# Revit family: lady_b_lady_b_585
name_source: partatom
category: Leuchten
revit_build: Autodesk Revit 2016 (Build: 20190508_0715(x64)
units: mm (PartAtom-declared; Revit-internal decimal feet)

## family parameters
Basisbauteil = Fläche
Beim Laden mit Abzugskörper schneiden = Nein
Bemaßung runder Anschluss = Durchmesser verwenden
Gemeinsam genutzt = Nein
Lichtquelle = Nein
Raumberechnungspunkt = Nein
Teiletyp = Normal

## types (1)
- BI (1 x LED, 4500 lm, 45 W, 3000K)
    Approval mark = CE
    Beschreibung = Extremely slight suspension lamp, suitable for domestic and professional environments.
Diffuser in smoothed material with double satin finish, 6mm thick, uniform lighting.
Available in two sizes, high efficiency LEDs.
Colors: white (BI), black (NE).

DIMMABLE ON DEMAND 
DRIVER INCLUDED LED 24V  CRI90
    CIE Flux Codes = 47 80 97 100 100
    Color Rendering = 1B
    Color Temperature = 3000K
    Height = 36 mm
    Hersteller = ICONE
    Lamp Light Flux = 4500 lm
    Lamp Power = 45 W
    Lamp count = 1
    Lampe = 1 x LED
    Length = 585 mm
    Lifetime = 50000 h
    Luminous efficacy = 100 lm/W
    ModVariant = Nein
    Modell = LADY B 585
    Mounting Place = Ceiling
    Mounting Type = Pendant
    Number of Poles = 1
    OnlyDefault = Ja
    Power Factor = 1
    Product Name = LADY B
    Product group = ceiling mounted luminaire
    ProductGroupID = 3
    Protection Class = Protection class I
    Protection Degree = IP 20
    RlxData = <blob elided: 122377 chars, md5=742b9786>
    Scheinlast = 45 VA
    Socket = socket
    Standby Power = 0 W
    System Light Flux = 4494 lm
    System Power = 45 W
    Typenbild = lady-b.jpg
    Typenkommentare = white
    URL = http://relux.com
    VarID = bi
    Voltage = 0 V
    Vorgabe-Ansicht = 1800 mm
    Weight = 0.00 kg
    Width = 0 mm  [stored 0 ft]

note: [stored X ft] marks values corroborated as IEEE doubles in the binary element streams (Revit-internal decimal feet)

## geometry (parser evidence)
native form markers: Blend x4, Sweep x15
no freeform markers — native parametric forms only
